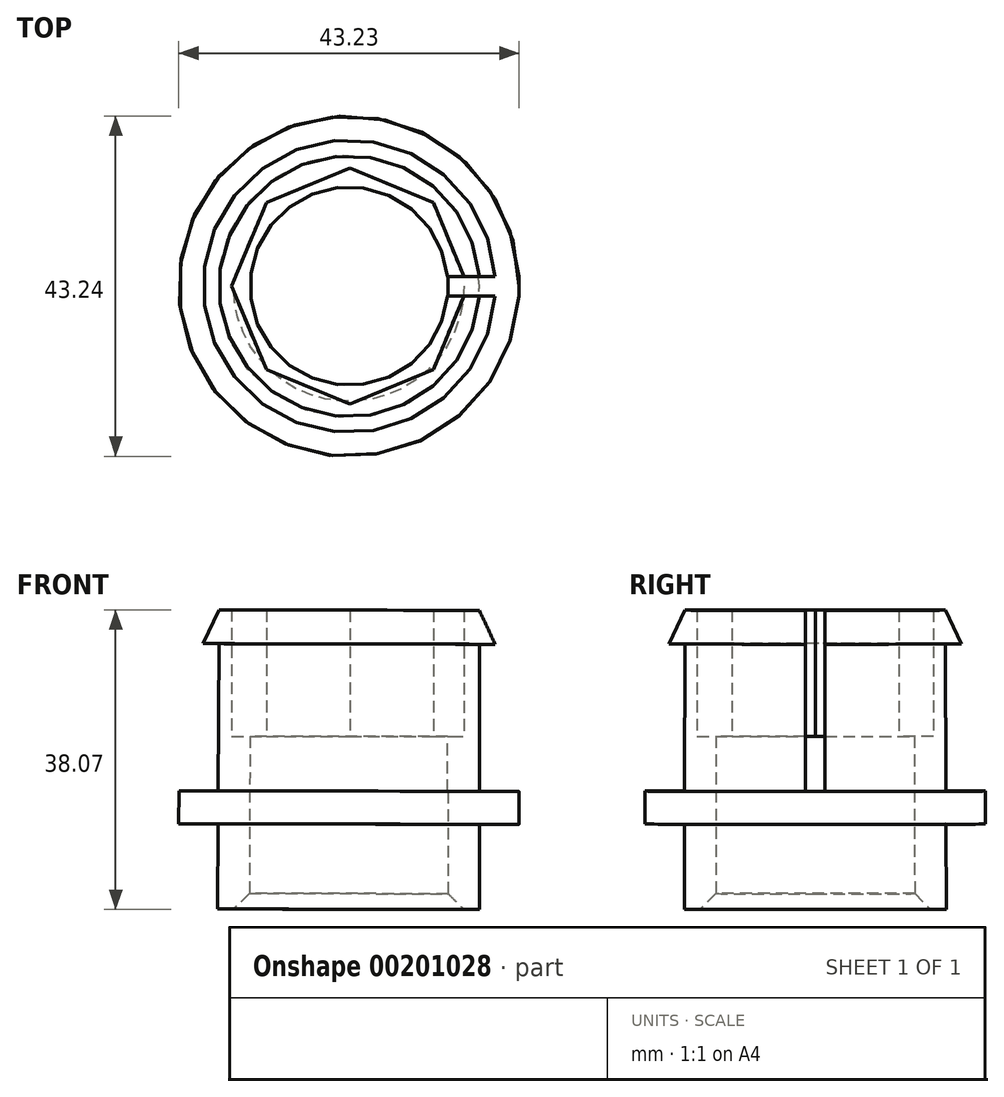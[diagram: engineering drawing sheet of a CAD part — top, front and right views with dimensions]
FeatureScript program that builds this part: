
annotation { "Feature Type Name" : "Feature", "Feature Type Description" : "" }
export const myFeature = defineFeature(function(context is Context, id is Id, definition is map)
    precondition{}
    {
        {
            var Q0;
            Q0=qCreatedBy(makeId("Front.planeOp"),FACE);
            var sketch = newSketch(context, id + "F0", { "sketchPlane" : qUnion([Q0])});
            skLineSegment(sketch, "E0", {"start": v(-38.84, 18) * mm, "end": v(38.55, 18) * mm, "construction": true});
            skLineSegment(sketch, "E1", {"start": v(12.5, 10) * mm, "end": v(12.5, -15) * mm});
            skLineSegment(sketch, "E2", {"start": v(12.5, -15) * mm, "end": v(16.5, -15) * mm});
            skLineSegment(sketch, "E3", {"start": v(16.5, -15) * mm, "end": v(16.5, -4.18) * mm});
            skLineSegment(sketch, "E4", {"start": v(16.5, 18.7) * mm, "end": v(18.5, 18.7) * mm});
            skLineSegment(sketch, "E5", {"start": v(18.5, 18.7) * mm, "end": v(16.5, 23) * mm});
            skLineSegment(sketch, "E6", {"start": v(16.5, 23) * mm, "end": v(12.5, 23) * mm});
            skLineSegment(sketch, "E7", {"start": v(16.5, -4.18) * mm, "end": v(21.5, -4.18) * mm});
            skLineSegment(sketch, "E8", {"start": v(21.5, -4.18) * mm, "end": v(21.5, 0) * mm});
            skLineSegment(sketch, "E9", {"start": v(21.5, 0) * mm, "end": v(16.5, 0) * mm});
            skLineSegment(sketch, "E10.trimOffspring", {"start": v(16.5, 0) * mm, "end": v(16.5, 18.7) * mm});
            skLineSegment(sketch, "E11", {"start": v(0, 49.35) * mm, "end": v(-0.14, -17.28) * mm, "construction": true});
            skPoint(sketch, "E11.endSnap0", {"position": v(-0.14, 18) * mm});
            skLineSegment(sketch, "E12", {"start": v(12.5, 23) * mm, "end": v(12.5, 10) * mm});
            skSolve(sketch);
        }
        {
            var Q0;
            Q0 = qSketchRegion(id + "F0", true);
            var Q1;
            Q1=sQuery(id+"F0.wireOp",EDGE,"E11");
            revolve(context, id + "F1", {"entities" : qUnion([Q0]), "axis" : qUnion([Q1]), "revolveType" : RevolveType.FULL});
        }
        {
            var Q0;
            Q0=qCreatedBy(makeId("Top.planeOp"),FACE);
            var sketch = newSketch(context, id + "F2", { "sketchPlane" : qUnion([Q0])});
            skLineSegment(sketch, "E13.bottom", {"start": v(6.53, 1.25) * mm, "end": v(27.86, 1.25) * mm});
            skLineSegment(sketch, "E13.top", {"start": v(6.53, -1.25) * mm, "end": v(27.86, -1.25) * mm});
            skLineSegment(sketch, "E13.left", {"start": v(6.53, 1.25) * mm, "end": v(6.53, -1.25) * mm});
            skLineSegment(sketch, "E13.right", {"start": v(27.86, 1.25) * mm, "end": v(27.86, -1.25) * mm});
            skSolve(sketch);
        }
        {
            var Q0;
            Q0 = qSketchRegion(id + "F2", true);
            extrude(context, id + "F3", {"entities" : qUnion([Q0]), "operationType" : NewBodyOperationType.REMOVE, "endBound" : BoundingType.THROUGH_ALL, "depth" : 25 * mm});
        }
        {
            var Q0;
            Q0=makeQuery(id+"F1.opRevolve","SWEPT_EDGE",EDGE,{"disambiguationData":[OSD([sQuery(id+"F0.wireOp",EDGE,"E1"),sQuery(id+"F0.wireOp",EDGE,"E2")])]});
            chamfer(context, id + "F4", {"entities" : qUnion([Q0]), "width" : 2 * mm, "tangentPropagation" : true});
        }
        {
            var Q0;
            Q0=qCreatedBy(makeId("Top.planeOp"),FACE);
            cPlane(context, id + "F5", {"entities" : qUnion([Q0]), "cplaneType" : CPlaneType.OFFSET, "offset" : 7 * mm, "width" : 150 * mm, "height" : 150 * mm});
        }
        {
            var Q0;
            Q0=qCreatedBy(id+"F5.planeOp",FACE);
            var sketch = newSketch(context, id + "F6", { "sketchPlane" : qUnion([Q0])});
            skCircle(sketch, "E14.cCircle", {"center": v(0, 0) * mm, "radius": 15 * mm, "construction": true});
            skLineSegment(sketch, "E14.0", {"start": v(0, 15) * mm, "end": v(10.6, 10.6) * mm});
            skLineSegment(sketch, "E14.1", {"start": v(10.6, 10.6) * mm, "end": v(15, 0) * mm});
            skLineSegment(sketch, "E14.2", {"start": v(15, 0) * mm, "end": v(10.6, -10.6) * mm});
            skLineSegment(sketch, "E14.3", {"start": v(10.6, -10.6) * mm, "end": v(0, -15) * mm});
            skLineSegment(sketch, "E14.4", {"start": v(0, -15) * mm, "end": v(-10.6, -10.6) * mm});
            skLineSegment(sketch, "E14.5", {"start": v(-10.6, -10.6) * mm, "end": v(-15, 0) * mm});
            skLineSegment(sketch, "E14.6", {"start": v(-15, 0) * mm, "end": v(-10.6, 10.6) * mm});
            skLineSegment(sketch, "E14.7", {"start": v(-10.6, 10.6) * mm, "end": v(0, 15) * mm});
            skSolve(sketch);
        }
        {
            var Q0;
            Q0 = qSketchRegion(id + "F6", true);
            extrude(context, id + "F7", {"entities" : qUnion([Q0]), "operationType" : NewBodyOperationType.REMOVE, "depth" : 25 * mm});
        }
    });
